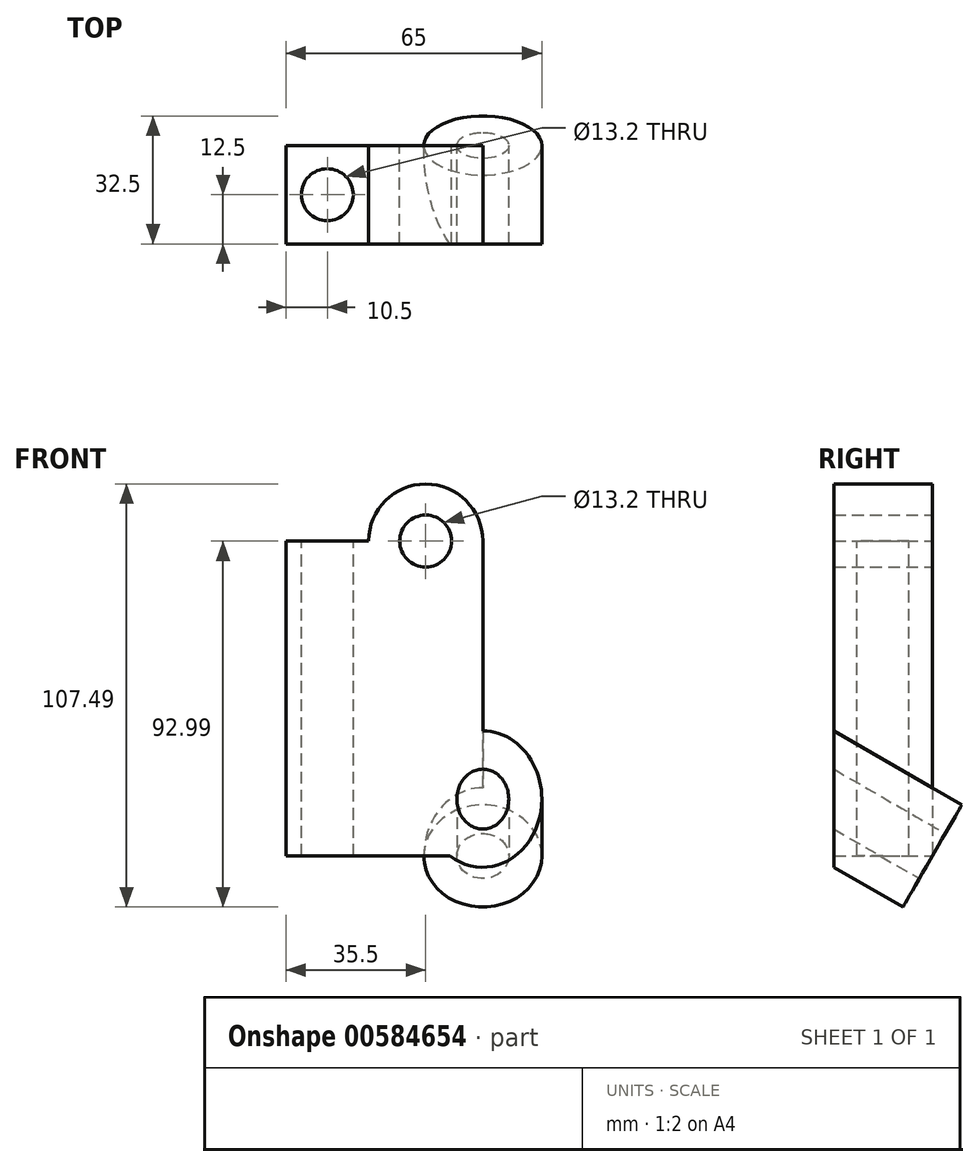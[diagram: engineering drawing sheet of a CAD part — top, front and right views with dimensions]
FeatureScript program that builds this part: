
annotation { "Feature Type Name" : "Feature", "Feature Type Description" : "" }
export const myFeature = defineFeature(function(context is Context, id is Id, definition is map)
    precondition{}
    {
        {
            var Q0;
            Q0=qCreatedBy(makeId("Front.planeOp"),FACE);
            var sketch = newSketch(context, id + "F0", { "sketchPlane" : qUnion([Q0])});
            skLineSegment(sketch, "E0.bottom", {"start": v(25, -40) * mm, "end": v(-25, -40) * mm});
            skLineSegment(sketch, "E0.top", {"start": v(25, 40) * mm, "end": v(-25, 40) * mm});
            skLineSegment(sketch, "E0.left", {"start": v(25, -40) * mm, "end": v(25, 40) * mm});
            skLineSegment(sketch, "E0.right", {"start": v(-25, -40) * mm, "end": v(-25, 40) * mm});
            skPoint(sketch, "E0.middle", {"position": v(0, 0) * mm});
            skCircle(sketch, "E1", {"center": v(10.5, 40) * mm, "radius": 14.5 * mm});
            skSolve(sketch);
        }
        {
            var Q0;
            Q0 = qSketchRegion(id + "F0", true);
            extrude(context, id + "F1", {"entities" : qUnion([Q0]), "depth" : 25 * mm, "offsetDistance" : 25 * mm});
        }
        {
            var Q0;
            Q0=makeQuery(id+"F1.opExtrude","CAP_FACE",FACE,{"disambiguationData":[OSD([sQuery(id+"F0.wireOp",EDGE,"E0.bottom"),sQuery(id+"F0.wireOp",EDGE,"E0.top"),sQuery(id+"F0.wireOp",EDGE,"E0.left"),sQuery(id+"F0.wireOp",EDGE,"E0.right"),sQuery(id+"F0.wireOp",EDGE,"E1")])],"isStart":true});
            var Q1;
            Q1=makeQuery(id+"F1.opExtrude","CAP_EDGE",EDGE,{"disambiguationData":[OSD([sQuery(id+"F0.wireOp",EDGE,"E0.bottom")])],"isStart":true});
            cPlane(context, id + "F2", {"entities" : qUnion([Q0, Q1]), "cplaneType" : CPlaneType.LINE_ANGLE, "offset" : 25 * mm, "angle" : 30 * degree, "width" : 150 * mm, "height" : 150 * mm});
        }
        {
            var Q0;
            Q0=qCreatedBy(id+"F2.planeOp",FACE);
            var sketch = newSketch(context, id + "F3", { "sketchPlane" : qUnion([Q0])});
            skCircle(sketch, "E2", {"center": v(25, -34.64) * mm, "radius": 15 * mm});
            skSolve(sketch);
        }
        {
            var Q0;
            Q0 = qSketchRegion(id + "F3", true);
            extrude(context, id + "F4", {"entities" : qUnion([Q0]), "operationType" : NewBodyOperationType.ADD, "depth" : 52 * mm, "offsetDistance" : 25 * mm});
        }
        {
            var Q0;
            Q0=makeQuery(id+"F4.opExtrude","CAP_FACE",FACE,{"disambiguationData":[OSD([sQuery(id+"F3.wireOp",EDGE,"E2")])],"isStart":true});
            var sketch = newSketch(context, id + "F5", { "sketchPlane" : qUnion([Q0])});
            skPoint(sketch, "E3", {"position": v(-25, -34.64) * mm});
            skSolve(sketch);
        }
        {
            var Q0;
            Q0=sQuery(id+"F5.wireOp",VERTEX,"E3");
            var Q1;
            Q1=makeQuery(id+"F1.opExtrude","SWEPT_BODY",BODY,{"disambiguationData":[OSD([sQuery(id+"F0.wireOp",EDGE,"E0.bottom"),sQuery(id+"F0.wireOp",EDGE,"E0.top"),sQuery(id+"F0.wireOp",EDGE,"E0.left"),sQuery(id+"F0.wireOp",EDGE,"E0.right"),sQuery(id+"F0.wireOp",EDGE,"E1")])]});
            hole(context, id + "F6", {"style" : HoleStyle.C_BORE, "endStyle" : HoleEndStyle.THROUGH, "holeDiameter" : 13.2 * mm, "cBoreDiameter" : 19.25 * mm, "cBoreDepth" : 0 * mm, "majorDiameter" : 5 * mm, "isTappedThrough" : true, "tappedDepth" : 12 * mm, "tapClearance" : 3, "startFromSketch" : true, "locations" : qUnion([Q0]), "scope" : qUnion([Q1])});
        }
        {
            var Q0;
            Q0=makeQuery(id+"F1.opExtrude","CAP_FACE",FACE,{"disambiguationData":[OSD([sQuery(id+"F0.wireOp",EDGE,"E0.bottom"),sQuery(id+"F0.wireOp",EDGE,"E0.top"),sQuery(id+"F0.wireOp",EDGE,"E0.left"),sQuery(id+"F0.wireOp",EDGE,"E0.right"),sQuery(id+"F0.wireOp",EDGE,"E1")])],"isStart":true});
            var sketch = newSketch(context, id + "F7", { "sketchPlane" : qUnion([Q0])});
            skPoint(sketch, "E4", {"position": v(-10.5, 40) * mm});
            skSolve(sketch);
        }
        {
            var Q0;
            Q0=sQuery(id+"F7.wireOp",VERTEX,"E4");
            var Q1;
            Q1=makeQuery(id+"F1.opExtrude","SWEPT_BODY",BODY,{"disambiguationData":[OSD([sQuery(id+"F0.wireOp",EDGE,"E0.bottom"),sQuery(id+"F0.wireOp",EDGE,"E0.top"),sQuery(id+"F0.wireOp",EDGE,"E0.left"),sQuery(id+"F0.wireOp",EDGE,"E0.right"),sQuery(id+"F0.wireOp",EDGE,"E1")])]});
            hole(context, id + "F8", {"style" : HoleStyle.C_BORE, "endStyle" : HoleEndStyle.THROUGH, "holeDiameter" : 13.2 * mm, "cBoreDiameter" : 19.25 * mm, "cBoreDepth" : 0 * mm, "majorDiameter" : 5 * mm, "isTappedThrough" : true, "tappedDepth" : 12 * mm, "tapClearance" : 3, "startFromSketch" : true, "locations" : qUnion([Q0]), "scope" : qUnion([Q1])});
        }
        {
            var Q0;
            Q0=makeQuery(id+"F1.opExtrude","SWEPT_FACE",FACE,{"disambiguationData":[OSD([sQuery(id+"F0.wireOp",EDGE,"E0.top")])]});
            var sketch = newSketch(context, id + "F9", { "sketchPlane" : qUnion([Q0])});
            skPoint(sketch, "E5", {"position": v(-14.5, -12.5) * mm});
            skPoint(sketch, "E5.positionSnap0", {"position": v(-4, -12.5) * mm});
            skSolve(sketch);
        }
        {
            var Q0;
            Q0=sQuery(id+"F9.wireOp",VERTEX,"E5");
            var Q1;
            Q1=makeQuery(id+"F1.opExtrude","SWEPT_BODY",BODY,{"disambiguationData":[OSD([sQuery(id+"F0.wireOp",EDGE,"E0.bottom"),sQuery(id+"F0.wireOp",EDGE,"E0.top"),sQuery(id+"F0.wireOp",EDGE,"E0.left"),sQuery(id+"F0.wireOp",EDGE,"E0.right"),sQuery(id+"F0.wireOp",EDGE,"E1")])]});
            hole(context, id + "F10", {"style" : HoleStyle.C_BORE, "endStyle" : HoleEndStyle.THROUGH, "holeDiameter" : 13.2 * mm, "cBoreDiameter" : 19.25 * mm, "cBoreDepth" : 0 * mm, "majorDiameter" : 5 * mm, "isTappedThrough" : true, "tappedDepth" : 12 * mm, "tapClearance" : 3, "startFromSketch" : true, "locations" : qUnion([Q0]), "scope" : qUnion([Q1])});
        }
        {
            var Q0;
            Q0=qCreatedBy(makeId("Right.planeOp"),FACE);
            var sketch = newSketch(context, id + "F11", { "sketchPlane" : qUnion([Q0])});
            skLineSegment(sketch, "E6.bottom", {"start": v(-25, 3.99) * mm, "end": v(-60.9, 3.99) * mm});
            skLineSegment(sketch, "E6.top", {"start": v(-25, -48.97) * mm, "end": v(-60.9, -48.97) * mm});
            skLineSegment(sketch, "E6.left", {"start": v(-25, 3.99) * mm, "end": v(-25, -48.97) * mm});
            skLineSegment(sketch, "E6.right", {"start": v(-60.9, 3.99) * mm, "end": v(-60.9, -48.97) * mm});
            skSolve(sketch);
        }
        {
            var Q0;
            Q0 = qSketchRegion(id + "F11", true);
            extrude(context, id + "F12", {"entities" : qUnion([Q0]), "operationType" : NewBodyOperationType.REMOVE, "depth" : 58 * mm, "offsetDistance" : 25 * mm});
        }
    });
